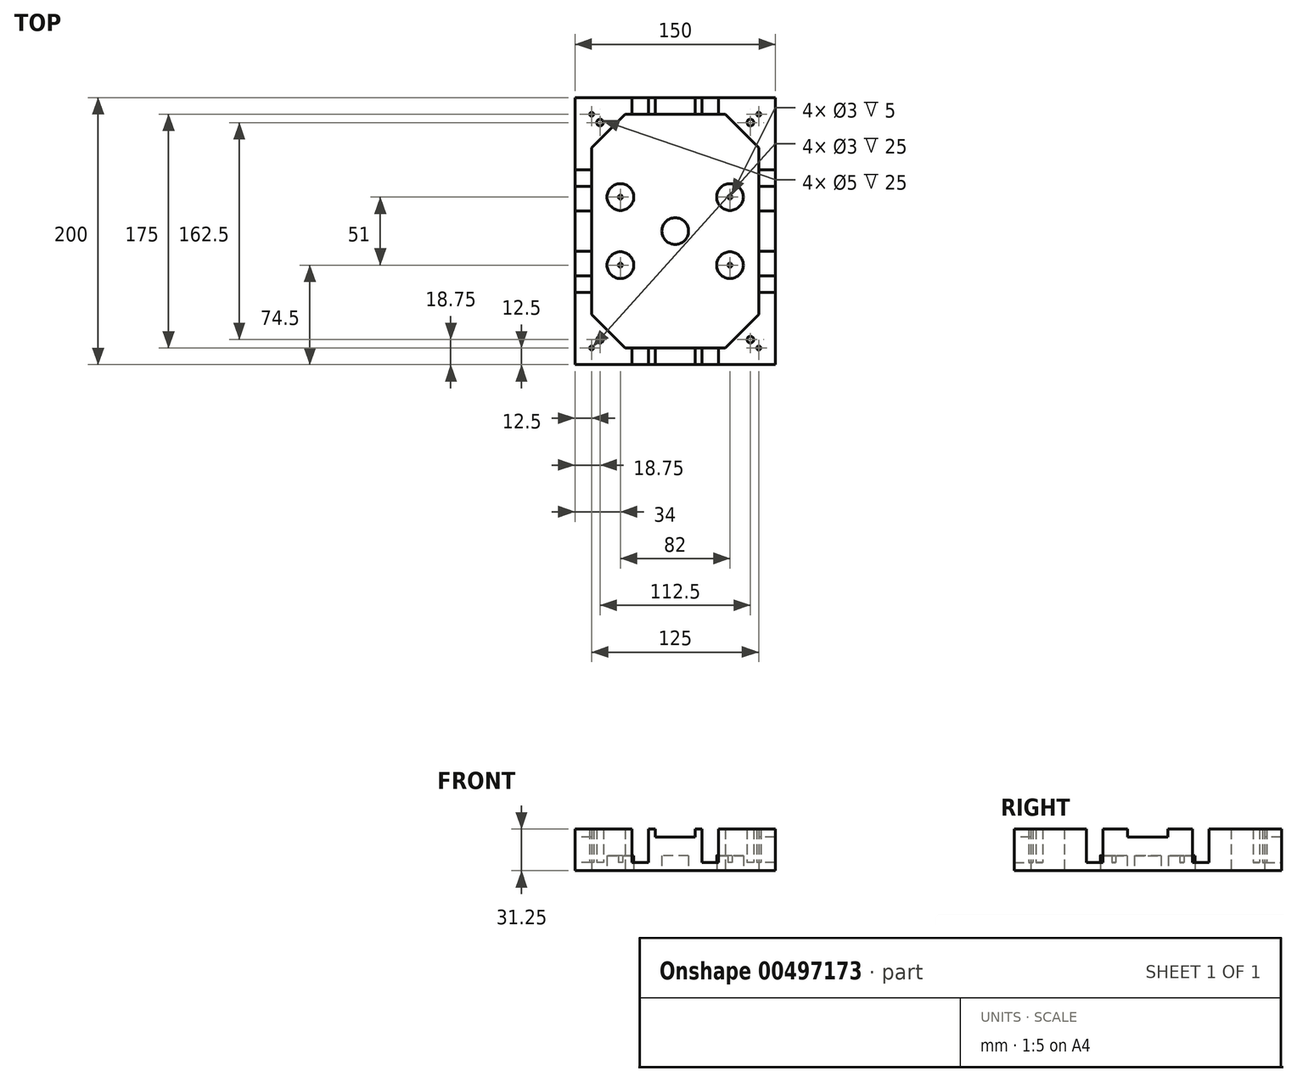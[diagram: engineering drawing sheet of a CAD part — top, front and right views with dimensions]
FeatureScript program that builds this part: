
annotation { "Feature Type Name" : "Feature", "Feature Type Description" : "" }
export const myFeature = defineFeature(function(context is Context, id is Id, definition is map)
    precondition{}
    {
        {
            var Q0;
            Q0=qCreatedBy(makeId("Top.planeOp"),FACE);
            var sketch = newSketch(context, id + "F0", { "sketchPlane" : qUnion([Q0])});
            skLineSegment(sketch, "E0.bottom", {"start": v(-75, 100) * mm, "end": v(75, 100) * mm});
            skLineSegment(sketch, "E0.top", {"start": v(-75, -100) * mm, "end": v(75, -100) * mm});
            skLineSegment(sketch, "E0.left", {"start": v(-75, 100) * mm, "end": v(-75, -100) * mm});
            skLineSegment(sketch, "E0.right", {"start": v(75, 100) * mm, "end": v(75, -100) * mm});
            skPoint(sketch, "E0.middle", {"position": v(0, 0) * mm});
            skLineSegment(sketch, "E1.bottom", {"start": v(-68.75, 93.75) * mm, "end": v(68.75, 93.75) * mm});
            skLineSegment(sketch, "E1.top", {"start": v(-68.75, -93.75) * mm, "end": v(68.75, -93.75) * mm});
            skLineSegment(sketch, "E1.left", {"start": v(-68.75, 93.75) * mm, "end": v(-68.75, -93.75) * mm});
            skLineSegment(sketch, "E1.right", {"start": v(68.75, 93.75) * mm, "end": v(68.75, -93.75) * mm});
            skLineSegment(sketch, "E2.bottom", {"start": v(-62.5, 87.5) * mm, "end": v(62.5, 87.5) * mm});
            skLineSegment(sketch, "E2.top", {"start": v(-62.5, -87.5) * mm, "end": v(62.5, -87.5) * mm});
            skLineSegment(sketch, "E2.left", {"start": v(-62.5, 87.5) * mm, "end": v(-62.5, -87.5) * mm});
            skLineSegment(sketch, "E2.right", {"start": v(62.5, 87.5) * mm, "end": v(62.5, -87.5) * mm});
            skLineSegment(sketch, "E3.bottom", {"start": v(-51, 35.5) * mm, "end": v(51, 35.5) * mm, "construction": true});
            skLineSegment(sketch, "E3.top", {"start": v(-51, -35.5) * mm, "end": v(51, -35.5) * mm, "construction": true});
            skLineSegment(sketch, "E3.left", {"start": v(-51, 35.5) * mm, "end": v(-51, -35.5) * mm, "construction": true});
            skLineSegment(sketch, "E3.right", {"start": v(51, 35.5) * mm, "end": v(51, -35.5) * mm, "construction": true});
            skPoint(sketch, "E4", {"position": v(37.5, 87.5) * mm});
            skPoint(sketch, "E5", {"position": v(37.5, -87.5) * mm});
            skPoint(sketch, "E6", {"position": v(-37.5, 87.5) * mm});
            skPoint(sketch, "E7", {"position": v(-37.5, -87.5) * mm});
            skPoint(sketch, "E8", {"position": v(-62.5, 62.5) * mm});
            skPoint(sketch, "E9", {"position": v(62.5, 62.5) * mm});
            skPoint(sketch, "E10", {"position": v(62.5, -62.5) * mm});
            skPoint(sketch, "E11", {"position": v(-62.5, -62.5) * mm});
            skPoint(sketch, "E12", {"position": v(-62.5, 87.5) * mm});
            skPoint(sketch, "E13", {"position": v(62.5, 87.5) * mm});
            skPoint(sketch, "E14", {"position": v(62.5, -87.5) * mm});
            skPoint(sketch, "E15", {"position": v(-62.5, -87.5) * mm});
            skLineSegment(sketch, "E16", {"start": v(-62.5, -62.5) * mm, "end": v(-37.5, -87.5) * mm});
            skLineSegment(sketch, "E17", {"start": v(37.5, -87.5) * mm, "end": v(62.5, -62.5) * mm});
            skLineSegment(sketch, "E18", {"start": v(62.5, 62.5) * mm, "end": v(37.5, 87.5) * mm});
            skLineSegment(sketch, "E19", {"start": v(-37.5, 87.5) * mm, "end": v(-62.5, 62.5) * mm});
            skPoint(sketch, "E20", {"position": v(-50, 75) * mm});
            skPoint(sketch, "E21", {"position": v(50, 75) * mm});
            skPoint(sketch, "E22", {"position": v(50, -75) * mm});
            skPoint(sketch, "E23", {"position": v(-50, -75) * mm});
            skLineSegment(sketch, "E24", {"start": v(-62.5, 87.5) * mm, "end": v(-50, 75) * mm, "construction": true});
            skLineSegment(sketch, "E25", {"start": v(62.5, 87.5) * mm, "end": v(50, 75) * mm, "construction": true});
            skLineSegment(sketch, "E26", {"start": v(62.5, -87.5) * mm, "end": v(50, -75) * mm, "construction": true});
            skLineSegment(sketch, "E27", {"start": v(-62.5, -87.5) * mm, "end": v(-50, -75) * mm, "construction": true});
            skPoint(sketch, "E28", {"position": v(-56.25, 81.25) * mm});
            skPoint(sketch, "E29", {"position": v(56.25, 81.25) * mm});
            skPoint(sketch, "E30", {"position": v(56.25, -81.25) * mm});
            skPoint(sketch, "E31", {"position": v(-56.25, -81.25) * mm});
            skLineSegment(sketch, "E32.bottom", {"start": v(-51, 35.5) * mm, "end": v(-41, 35.5) * mm, "construction": true});
            skLineSegment(sketch, "E32.top", {"start": v(-51, 25.5) * mm, "end": v(-41, 25.5) * mm, "construction": true});
            skLineSegment(sketch, "E32.left", {"start": v(-51, 35.5) * mm, "end": v(-51, 25.5) * mm, "construction": true});
            skLineSegment(sketch, "E32.right", {"start": v(-41, 35.5) * mm, "end": v(-41, 25.5) * mm, "construction": true});
            skLineSegment(sketch, "E33.bottom", {"start": v(51, 35.5) * mm, "end": v(41, 35.5) * mm, "construction": true});
            skLineSegment(sketch, "E33.top", {"start": v(51, 25.5) * mm, "end": v(41, 25.5) * mm, "construction": true});
            skLineSegment(sketch, "E33.left", {"start": v(51, 35.5) * mm, "end": v(51, 25.5) * mm, "construction": true});
            skLineSegment(sketch, "E33.right", {"start": v(41, 35.5) * mm, "end": v(41, 25.5) * mm, "construction": true});
            skLineSegment(sketch, "E34.bottom", {"start": v(-51, -35.5) * mm, "end": v(-41, -35.5) * mm, "construction": true});
            skLineSegment(sketch, "E34.top", {"start": v(-51, -25.5) * mm, "end": v(-41, -25.5) * mm, "construction": true});
            skLineSegment(sketch, "E34.left", {"start": v(-51, -35.5) * mm, "end": v(-51, -25.5) * mm, "construction": true});
            skLineSegment(sketch, "E34.right", {"start": v(-41, -35.5) * mm, "end": v(-41, -25.5) * mm, "construction": true});
            skLineSegment(sketch, "E35.bottom", {"start": v(51, -35.5) * mm, "end": v(41, -35.5) * mm, "construction": true});
            skLineSegment(sketch, "E35.top", {"start": v(51, -25.5) * mm, "end": v(41, -25.5) * mm, "construction": true});
            skLineSegment(sketch, "E35.left", {"start": v(51, -35.5) * mm, "end": v(51, -25.5) * mm, "construction": true});
            skLineSegment(sketch, "E35.right", {"start": v(41, -35.5) * mm, "end": v(41, -25.5) * mm, "construction": true});
            skPoint(sketch, "E36", {"position": v(-41, 25.5) * mm});
            skPoint(sketch, "E37", {"position": v(41, 25.5) * mm});
            skPoint(sketch, "E38", {"position": v(41, -25.5) * mm});
            skPoint(sketch, "E39", {"position": v(-41, -25.5) * mm});
            skCircle(sketch, "E40", {"center": v(41, 25.5) * mm, "radius": 10 * mm});
            skCircle(sketch, "E41", {"center": v(-41, 25.5) * mm, "radius": 10 * mm});
            skCircle(sketch, "E42", {"center": v(-41, -25.5) * mm, "radius": 10 * mm});
            skCircle(sketch, "E43", {"center": v(41, -25.5) * mm, "radius": 10 * mm});
            skCircle(sketch, "E44", {"center": v(41, 25.5) * mm, "radius": 1.5 * mm});
            skCircle(sketch, "E45", {"center": v(-41, 25.5) * mm, "radius": 1.5 * mm});
            skCircle(sketch, "E46", {"center": v(-41, -25.5) * mm, "radius": 1.5 * mm});
            skCircle(sketch, "E47", {"center": v(41, -25.5) * mm, "radius": 1.5 * mm});
            skCircle(sketch, "E48", {"center": v(0, 0) * mm, "radius": 10 * mm});
            skCircle(sketch, "E49", {"center": v(-62.5, 87.5) * mm, "radius": 1.5 * mm});
            skCircle(sketch, "E50", {"center": v(62.5, 87.5) * mm, "radius": 1.5 * mm});
            skCircle(sketch, "E51", {"center": v(62.5, -87.5) * mm, "radius": 1.5 * mm});
            skCircle(sketch, "E52", {"center": v(-62.5, -87.5) * mm, "radius": 1.5 * mm});
            skCircle(sketch, "E53", {"center": v(-56.25, -81.25) * mm, "radius": 2.5 * mm});
            skCircle(sketch, "E54", {"center": v(56.25, -81.25) * mm, "radius": 2.5 * mm});
            skCircle(sketch, "E55", {"center": v(56.25, 81.25) * mm, "radius": 2.5 * mm});
            skCircle(sketch, "E56", {"center": v(-56.25, 81.25) * mm, "radius": 2.5 * mm});
            skPoint(sketch, "E57", {"position": v(0, 74.98) * mm});
            skPoint(sketch, "E58", {"position": v(15, -87.5) * mm});
            skPoint(sketch, "E59", {"position": v(15, -100) * mm});
            skPoint(sketch, "E60", {"position": v(-15, -100) * mm});
            skPoint(sketch, "E61", {"position": v(-15, -87.5) * mm});
            skLineSegment(sketch, "E62", {"start": v(-15, -87.5) * mm, "end": v(-15, -100) * mm});
            skLineSegment(sketch, "E63", {"start": v(15, -87.5) * mm, "end": v(15, -100) * mm});
            skPoint(sketch, "E64", {"position": v(32.5, -87.5) * mm});
            skPoint(sketch, "E65", {"position": v(32.5, -100) * mm});
            skPoint(sketch, "E66", {"position": v(20, -100) * mm});
            skPoint(sketch, "E67", {"position": v(20, -87.5) * mm});
            skPoint(sketch, "E68", {"position": v(-20, -87.5) * mm});
            skPoint(sketch, "E69", {"position": v(-32.5, -87.5) * mm});
            skPoint(sketch, "E70", {"position": v(-32.5, -100) * mm});
            skPoint(sketch, "E71", {"position": v(-20, -100) * mm});
            skPoint(sketch, "E72", {"position": v(-15, 87.5) * mm});
            skPoint(sketch, "E73", {"position": v(-20, 87.5) * mm});
            skPoint(sketch, "E74", {"position": v(-32.5, 87.5) * mm});
            skPoint(sketch, "E75", {"position": v(32.5, 87.5) * mm});
            skPoint(sketch, "E76", {"position": v(20, 87.5) * mm});
            skPoint(sketch, "E77", {"position": v(15, 87.5) * mm});
            skPoint(sketch, "E78", {"position": v(-32.5, 100) * mm});
            skPoint(sketch, "E79", {"position": v(-20, 100) * mm});
            skPoint(sketch, "E80", {"position": v(-15, 100) * mm});
            skPoint(sketch, "E81", {"position": v(15, 100) * mm});
            skPoint(sketch, "E82", {"position": v(20, 100) * mm});
            skPoint(sketch, "E83", {"position": v(32.5, 100) * mm});
            skPoint(sketch, "E84", {"position": v(75, 15) * mm});
            skPoint(sketch, "E85", {"position": v(75, -15) * mm});
            skPoint(sketch, "E86", {"position": v(-75, -15) * mm});
            skPoint(sketch, "E87", {"position": v(-75, 15) * mm});
            skPoint(sketch, "E88", {"position": v(62.5, 15) * mm});
            skPoint(sketch, "E89", {"position": v(62.5, -15) * mm});
            skPoint(sketch, "E90", {"position": v(-62.5, 15) * mm});
            skPoint(sketch, "E91", {"position": v(-62.5, -15) * mm});
            skLineSegment(sketch, "E92", {"start": v(-32.5, 100) * mm, "end": v(-32.5, 87.5) * mm});
            skLineSegment(sketch, "E93", {"start": v(-20, 100) * mm, "end": v(-20, 87.5) * mm});
            skLineSegment(sketch, "E94", {"start": v(-15, 100) * mm, "end": v(-15, 87.5) * mm});
            skLineSegment(sketch, "E95", {"start": v(15, 100) * mm, "end": v(15, 87.5) * mm});
            skLineSegment(sketch, "E96", {"start": v(20, 100) * mm, "end": v(20, 87.5) * mm});
            skLineSegment(sketch, "E97", {"start": v(32.5, 100) * mm, "end": v(32.5, 87.5) * mm});
            skLineSegment(sketch, "E98", {"start": v(75, 15) * mm, "end": v(62.5, 15) * mm});
            skLineSegment(sketch, "E99", {"start": v(75, -15) * mm, "end": v(62.5, -15) * mm});
            skLineSegment(sketch, "E100", {"start": v(-62.5, 15) * mm, "end": v(-75, 15) * mm});
            skLineSegment(sketch, "E101", {"start": v(-62.5, -15) * mm, "end": v(-75, -15) * mm});
            skLineSegment(sketch, "E102", {"start": v(-32.5, -87.5) * mm, "end": v(-32.5, -100) * mm});
            skLineSegment(sketch, "E103", {"start": v(-20, -87.5) * mm, "end": v(-20, -100) * mm});
            skLineSegment(sketch, "E104", {"start": v(20, -87.5) * mm, "end": v(20, -100) * mm});
            skLineSegment(sketch, "E105", {"start": v(32.5, -87.5) * mm, "end": v(32.5, -100) * mm});
            skPoint(sketch, "E106", {"position": v(62.5, 46) * mm});
            skPoint(sketch, "E107", {"position": v(62.5, 33.5) * mm});
            skPoint(sketch, "E108", {"position": v(62.5, -46) * mm});
            skPoint(sketch, "E109", {"position": v(62.5, -33.5) * mm});
            skPoint(sketch, "E110", {"position": v(-62.5, 46) * mm});
            skPoint(sketch, "E111", {"position": v(-62.5, 33.5) * mm});
            skPoint(sketch, "E112", {"position": v(-62.5, -33.5) * mm});
            skPoint(sketch, "E113", {"position": v(-62.5, -46) * mm});
            skPoint(sketch, "E114", {"position": v(-75, 46) * mm});
            skPoint(sketch, "E115", {"position": v(-75, 33.5) * mm});
            skPoint(sketch, "E116", {"position": v(-75, -33.5) * mm});
            skPoint(sketch, "E117", {"position": v(-75, -46) * mm});
            skPoint(sketch, "E118", {"position": v(75, -46) * mm});
            skPoint(sketch, "E119", {"position": v(75, -33.5) * mm});
            skPoint(sketch, "E120", {"position": v(75, 46) * mm});
            skPoint(sketch, "E121", {"position": v(75, 33.5) * mm});
            skLineSegment(sketch, "E122", {"start": v(-75, 46) * mm, "end": v(-62.5, 46) * mm});
            skLineSegment(sketch, "E123", {"start": v(-75, 33.5) * mm, "end": v(-62.5, 33.5) * mm});
            skLineSegment(sketch, "E124", {"start": v(-75, -33.5) * mm, "end": v(-62.5, -33.5) * mm});
            skLineSegment(sketch, "E125", {"start": v(-75, -46) * mm, "end": v(-62.5, -46) * mm});
            skLineSegment(sketch, "E126", {"start": v(62.5, -33.5) * mm, "end": v(75, -33.5) * mm});
            skLineSegment(sketch, "E127", {"start": v(62.5, -46) * mm, "end": v(75, -46) * mm});
            skLineSegment(sketch, "E128", {"start": v(62.5, 46) * mm, "end": v(75, 46) * mm});
            skPoint(sketch, "E129", {"position": v(-32.5, 93.75) * mm});
            skPoint(sketch, "E130", {"position": v(-20, 93.75) * mm});
            skPoint(sketch, "E131", {"position": v(-15, 93.75) * mm});
            skPoint(sketch, "E132", {"position": v(15, 93.75) * mm});
            skPoint(sketch, "E133", {"position": v(20, 93.75) * mm});
            skPoint(sketch, "E134", {"position": v(32.5, 93.75) * mm});
            skPoint(sketch, "E135", {"position": v(68.75, 46) * mm});
            skPoint(sketch, "E136", {"position": v(68.75, 33.5) * mm});
            skPoint(sketch, "E137", {"position": v(68.75, 15) * mm});
            skPoint(sketch, "E138", {"position": v(68.75, -15) * mm});
            skPoint(sketch, "E139", {"position": v(68.75, -33.5) * mm});
            skPoint(sketch, "E140", {"position": v(68.75, -46) * mm});
            skPoint(sketch, "E141", {"position": v(32.5, -93.75) * mm});
            skPoint(sketch, "E142", {"position": v(20, -93.75) * mm});
            skPoint(sketch, "E143", {"position": v(15, -93.75) * mm});
            skPoint(sketch, "E144", {"position": v(-15, -93.75) * mm});
            skPoint(sketch, "E145", {"position": v(-20, -93.75) * mm});
            skPoint(sketch, "E146", {"position": v(-32.5, -93.75) * mm});
            skPoint(sketch, "E147", {"position": v(-68.75, -46) * mm});
            skPoint(sketch, "E148", {"position": v(-68.75, -33.5) * mm});
            skPoint(sketch, "E149", {"position": v(-68.75, -15) * mm});
            skPoint(sketch, "E150", {"position": v(-68.75, 15) * mm});
            skPoint(sketch, "E151", {"position": v(-68.75, 33.5) * mm});
            skPoint(sketch, "E152", {"position": v(-68.75, 46) * mm});
            skLineSegment(sketch, "E153", {"start": v(75, 33.5) * mm, "end": v(62.5, 33.5) * mm});
            skSolve(sketch);
        }
        {
            var Q0;
            Q0=makeQuery(id+"F0.imprint","IMPRINT",FACE,{"disambiguationData":[TD([[makeQuery(id+"F0.imprint","IMPRINT",EDGE,{"derivedFrom":sQuery(id+"F0.wireOp",EDGE,"E43")}),1.0]])]});
            var Q1;
            Q1=makeQuery(id+"F0.imprint","IMPRINT",FACE,{"disambiguationData":[TD([[makeQuery(id+"F0.imprint","IMPRINT",EDGE,{"derivedFrom":sQuery(id+"F0.wireOp",EDGE,"E42")}),1.0]])]});
            var Q2;
            {var subQ5=sQuery(id+"F0.wireOp",EDGE,"E17");Q2=makeQuery(id+"F0.imprint","IMPRINT",FACE,{"disambiguationData":[TD([[makeQuery(id+"F0.imprint","IMPRINT",EDGE,{"derivedFrom":subQ5}),-1.0]])]});}
            var Q3;
            {var subQ0=sQuery(id+"F0.wireOp",EDGE,"E122");var subQ1=sQuery(id+"F0.wireOp",EDGE,"E0.left");var subQ2=makeQuery(id+"F0.imprint","INTERSECT",VERTEX,{"derivedFrom":[subQ1,subQ0]});Q3=makeQuery(id+"F0.imprint","IMPRINT",FACE,{"disambiguationData":[TD([[makeQuery(id+"F0.imprint","IMPRINT",EDGE,{"disambiguationData":[TD([[subQ2,-1.0]])],"derivedFrom":subQ1}),1.0]])]});}
            var Q4;
            {var subQ0=sQuery(id+"F0.wireOp",EDGE,"E124");var subQ1=sQuery(id+"F0.wireOp",EDGE,"E0.left");var subQ2=makeQuery(id+"F0.imprint","INTERSECT",VERTEX,{"derivedFrom":[subQ1,subQ0]});Q4=makeQuery(id+"F0.imprint","IMPRINT",FACE,{"disambiguationData":[TD([[makeQuery(id+"F0.imprint","IMPRINT",EDGE,{"disambiguationData":[TD([[subQ2,-1.0]])],"derivedFrom":subQ1}),1.0]])]});}
            var Q5;
            {var subQ0=sQuery(id+"F0.wireOp",EDGE,"E62");var subQ1=sQuery(id+"F0.wireOp",EDGE,"E1.top");var subQ2=makeQuery(id+"F0.imprint","INTERSECT",VERTEX,{"derivedFrom":[subQ1,subQ0]});Q5=makeQuery(id+"F0.imprint","IMPRINT",FACE,{"disambiguationData":[TD([[makeQuery(id+"F0.imprint","IMPRINT",EDGE,{"disambiguationData":[TD([[subQ2,-1.0]])],"derivedFrom":subQ1}),1.0]])]});}
            var Q6;
            {var subQ0=sQuery(id+"F0.wireOp",EDGE,"E100");var subQ1=sQuery(id+"F0.wireOp",EDGE,"E0.left");var subQ2=makeQuery(id+"F0.imprint","INTERSECT",VERTEX,{"derivedFrom":[subQ1,subQ0]});Q6=makeQuery(id+"F0.imprint","IMPRINT",FACE,{"disambiguationData":[TD([[makeQuery(id+"F0.imprint","IMPRINT",EDGE,{"disambiguationData":[TD([[subQ2,-1.0]])],"derivedFrom":subQ1}),1.0]])]});}
            var Q7;
            {var subQ0=sQuery(id+"F0.wireOp",EDGE,"E62");var subQ1=sQuery(id+"F0.wireOp",EDGE,"E0.top");var subQ2=makeQuery(id+"F0.imprint","INTERSECT",VERTEX,{"derivedFrom":[subQ1,subQ0]});Q7=makeQuery(id+"F0.imprint","IMPRINT",FACE,{"disambiguationData":[TD([[makeQuery(id+"F0.imprint","IMPRINT",EDGE,{"disambiguationData":[TD([[subQ2,1.0]])],"derivedFrom":subQ1}),1.0]])]});}
            var Q8;
            {var subQ0=sQuery(id+"F0.wireOp",EDGE,"E99");var subQ1=sQuery(id+"F0.wireOp",EDGE,"E0.right");var subQ2=makeQuery(id+"F0.imprint","INTERSECT",VERTEX,{"derivedFrom":[subQ1,subQ0]});Q8=makeQuery(id+"F0.imprint","IMPRINT",FACE,{"disambiguationData":[TD([[makeQuery(id+"F0.imprint","IMPRINT",EDGE,{"disambiguationData":[TD([[subQ2,-1.0]])],"derivedFrom":subQ1}),-1.0]])]});}
            var Q9;
            {var subQ0=sQuery(id+"F0.wireOp",EDGE,"E98");var subQ1=sQuery(id+"F0.wireOp",EDGE,"E0.right");var subQ2=makeQuery(id+"F0.imprint","INTERSECT",VERTEX,{"derivedFrom":[subQ1,subQ0]});Q9=makeQuery(id+"F0.imprint","IMPRINT",FACE,{"disambiguationData":[TD([[makeQuery(id+"F0.imprint","IMPRINT",EDGE,{"disambiguationData":[TD([[subQ2,-1.0]])],"derivedFrom":subQ1}),-1.0]])]});}
            var Q10;
            {var subQ0=sQuery(id+"F0.wireOp",EDGE,"E94");var subQ1=sQuery(id+"F0.wireOp",EDGE,"E1.bottom");var subQ2=makeQuery(id+"F0.imprint","INTERSECT",VERTEX,{"derivedFrom":[subQ1,subQ0]});Q10=makeQuery(id+"F0.imprint","IMPRINT",FACE,{"disambiguationData":[TD([[makeQuery(id+"F0.imprint","IMPRINT",EDGE,{"disambiguationData":[TD([[subQ2,-1.0]])],"derivedFrom":subQ1}),-1.0]])]});}
            var Q11;
            {var subQ23=sQuery(id+"F0.wireOp",EDGE,"E16");Q11=makeQuery(id+"F0.imprint","IMPRINT",FACE,{"disambiguationData":[TD([[makeQuery(id+"F0.imprint","IMPRINT",EDGE,{"derivedFrom":subQ23}),1.0]])]});}
            var Q12;
            {var subQ0=sQuery(id+"F0.wireOp",EDGE,"E100");var subQ1=sQuery(id+"F0.wireOp",EDGE,"E0.left");var subQ2=makeQuery(id+"F0.imprint","INTERSECT",VERTEX,{"derivedFrom":[subQ1,subQ0]});Q12=makeQuery(id+"F0.imprint","IMPRINT",FACE,{"disambiguationData":[TD([[makeQuery(id+"F0.imprint","IMPRINT",EDGE,{"disambiguationData":[TD([[subQ2,1.0]])],"derivedFrom":subQ1}),1.0]])]});}
            var Q13;
            {var subQ0=sQuery(id+"F0.wireOp",EDGE,"E96");var subQ1=sQuery(id+"F0.wireOp",EDGE,"E0.bottom");var subQ2=makeQuery(id+"F0.imprint","INTERSECT",VERTEX,{"derivedFrom":[subQ1,subQ0]});Q13=makeQuery(id+"F0.imprint","IMPRINT",FACE,{"disambiguationData":[TD([[makeQuery(id+"F0.imprint","IMPRINT",EDGE,{"disambiguationData":[TD([[subQ2,-1.0]])],"derivedFrom":subQ1}),-1.0]])]});}
            var Q14;
            Q14=makeQuery(id+"F0.imprint","IMPRINT",FACE,{"disambiguationData":[TD([[makeQuery(id+"F0.imprint","IMPRINT",EDGE,{"derivedFrom":sQuery(id+"F0.wireOp",EDGE,"E41")}),1.0]])]});
            var Q15;
            {var subQ5=sQuery(id+"F0.wireOp",EDGE,"E16");Q15=makeQuery(id+"F0.imprint","IMPRINT",FACE,{"disambiguationData":[TD([[makeQuery(id+"F0.imprint","IMPRINT",EDGE,{"derivedFrom":subQ5}),-1.0]])]});}
            var Q16;
            {var subQ0=sQuery(id+"F0.wireOp",EDGE,"E95");var subQ1=sQuery(id+"F0.wireOp",EDGE,"E0.bottom");var subQ2=makeQuery(id+"F0.imprint","INTERSECT",VERTEX,{"derivedFrom":[subQ1,subQ0]});Q16=makeQuery(id+"F0.imprint","IMPRINT",FACE,{"disambiguationData":[TD([[makeQuery(id+"F0.imprint","IMPRINT",EDGE,{"disambiguationData":[TD([[subQ2,-1.0]])],"derivedFrom":subQ1}),-1.0]])]});}
            var Q17;
            {var subQ0=sQuery(id+"F0.wireOp",EDGE,"E102");var subQ1=sQuery(id+"F0.wireOp",EDGE,"E0.top");var subQ2=makeQuery(id+"F0.imprint","INTERSECT",VERTEX,{"derivedFrom":[subQ1,subQ0]});Q17=makeQuery(id+"F0.imprint","IMPRINT",FACE,{"disambiguationData":[TD([[makeQuery(id+"F0.imprint","IMPRINT",EDGE,{"disambiguationData":[TD([[subQ2,-1.0]])],"derivedFrom":subQ1}),1.0]])]});}
            var Q18;
            {var subQ0=sQuery(id+"F0.wireOp",EDGE,"E101");var subQ1=sQuery(id+"F0.wireOp",EDGE,"E1.left");var subQ2=makeQuery(id+"F0.imprint","INTERSECT",VERTEX,{"derivedFrom":[subQ1,subQ0]});Q18=makeQuery(id+"F0.imprint","IMPRINT",FACE,{"disambiguationData":[TD([[makeQuery(id+"F0.imprint","IMPRINT",EDGE,{"disambiguationData":[TD([[subQ2,-1.0]])],"derivedFrom":subQ1}),1.0]])]});}
            var Q19;
            {var subQ0=sQuery(id+"F0.wireOp",EDGE,"E99");var subQ1=sQuery(id+"F0.wireOp",EDGE,"E1.right");var subQ2=makeQuery(id+"F0.imprint","INTERSECT",VERTEX,{"derivedFrom":[subQ1,subQ0]});Q19=makeQuery(id+"F0.imprint","IMPRINT",FACE,{"disambiguationData":[TD([[makeQuery(id+"F0.imprint","IMPRINT",EDGE,{"disambiguationData":[TD([[subQ2,-1.0]])],"derivedFrom":subQ1}),-1.0]])]});}
            var Q20;
            {var subQ0=sQuery(id+"F0.wireOp",EDGE,"E103");var subQ1=sQuery(id+"F0.wireOp",EDGE,"E1.top");var subQ2=makeQuery(id+"F0.imprint","INTERSECT",VERTEX,{"derivedFrom":[subQ1,subQ0]});Q20=makeQuery(id+"F0.imprint","IMPRINT",FACE,{"disambiguationData":[TD([[makeQuery(id+"F0.imprint","IMPRINT",EDGE,{"disambiguationData":[TD([[subQ2,-1.0]])],"derivedFrom":subQ1}),1.0]])]});}
            var Q21;
            {var subQ0=sQuery(id+"F0.wireOp",EDGE,"E153");var subQ1=sQuery(id+"F0.wireOp",EDGE,"E1.right");var subQ2=makeQuery(id+"F0.imprint","INTERSECT",VERTEX,{"derivedFrom":[subQ1,subQ0]});Q21=makeQuery(id+"F0.imprint","IMPRINT",FACE,{"disambiguationData":[TD([[makeQuery(id+"F0.imprint","IMPRINT",EDGE,{"disambiguationData":[TD([[subQ2,-1.0]])],"derivedFrom":subQ1}),-1.0]])]});}
            var Q22;
            {var subQ7=sQuery(id+"F0.wireOp",EDGE,"E0.right");var subQ8=sQuery(id+"F0.wireOp",EDGE,"E0.top");var subQ9=makeQuery(id+"F0.imprint","INTERSECT",VERTEX,{"derivedFrom":[subQ8,subQ7]});Q22=makeQuery(id+"F0.imprint","IMPRINT",FACE,{"disambiguationData":[TD([[makeQuery(id+"F0.imprint","IMPRINT",EDGE,{"disambiguationData":[TD([[subQ9,1.0]])],"derivedFrom":subQ8}),1.0]])]});}
            var Q23;
            {var subQ0=sQuery(id+"F0.wireOp",EDGE,"E92");var subQ1=sQuery(id+"F0.wireOp",EDGE,"E1.bottom");var subQ2=makeQuery(id+"F0.imprint","INTERSECT",VERTEX,{"derivedFrom":[subQ1,subQ0]});Q23=makeQuery(id+"F0.imprint","IMPRINT",FACE,{"disambiguationData":[TD([[makeQuery(id+"F0.imprint","IMPRINT",EDGE,{"disambiguationData":[TD([[subQ2,-1.0]])],"derivedFrom":subQ1}),-1.0]])]});}
            var Q24;
            {var subQ0=sQuery(id+"F0.wireOp",EDGE,"E124");var subQ1=sQuery(id+"F0.wireOp",EDGE,"E1.left");var subQ2=makeQuery(id+"F0.imprint","INTERSECT",VERTEX,{"derivedFrom":[subQ1,subQ0]});Q24=makeQuery(id+"F0.imprint","IMPRINT",FACE,{"disambiguationData":[TD([[makeQuery(id+"F0.imprint","IMPRINT",EDGE,{"disambiguationData":[TD([[subQ2,-1.0]])],"derivedFrom":subQ1}),1.0]])]});}
            var Q25;
            {var subQ5=sQuery(id+"F0.wireOp",EDGE,"E0.right");var subQ9=sQuery(id+"F0.wireOp",EDGE,"E0.bottom");var subQ10=makeQuery(id+"F0.imprint","INTERSECT",VERTEX,{"derivedFrom":[subQ9,subQ5]});Q25=makeQuery(id+"F0.imprint","IMPRINT",FACE,{"disambiguationData":[TD([[makeQuery(id+"F0.imprint","IMPRINT",EDGE,{"disambiguationData":[TD([[subQ10,1.0]])],"derivedFrom":subQ9}),-1.0]])]});}
            var Q26;
            {var subQ0=sQuery(id+"F0.wireOp",EDGE,"E18");Q26=makeQuery(id+"F0.imprint","IMPRINT",FACE,{"disambiguationData":[TD([[makeQuery(id+"F0.imprint","IMPRINT",EDGE,{"derivedFrom":subQ0}),-1.0]])]});}
            var Q27;
            {var subQ7=sQuery(id+"F0.wireOp",EDGE,"E0.left");var subQ8=sQuery(id+"F0.wireOp",EDGE,"E0.bottom");var subQ9=makeQuery(id+"F0.imprint","INTERSECT",VERTEX,{"derivedFrom":[subQ8,subQ7]});Q27=makeQuery(id+"F0.imprint","IMPRINT",FACE,{"disambiguationData":[TD([[makeQuery(id+"F0.imprint","IMPRINT",EDGE,{"disambiguationData":[TD([[subQ9,-1.0]])],"derivedFrom":subQ8}),-1.0]])]});}
            var Q28;
            {var subQ8=sQuery(id+"F0.wireOp",EDGE,"E1.left");var subQ9=sQuery(id+"F0.wireOp",EDGE,"E1.bottom");var subQ10=makeQuery(id+"F0.imprint","INTERSECT",VERTEX,{"derivedFrom":[subQ9,subQ8]});Q28=makeQuery(id+"F0.imprint","IMPRINT",FACE,{"disambiguationData":[TD([[makeQuery(id+"F0.imprint","IMPRINT",EDGE,{"disambiguationData":[TD([[subQ10,-1.0]])],"derivedFrom":subQ9}),-1.0]])]});}
            var Q29;
            {var subQ0=sQuery(id+"F0.wireOp",EDGE,"E102");var subQ1=sQuery(id+"F0.wireOp",EDGE,"E1.top");var subQ2=makeQuery(id+"F0.imprint","INTERSECT",VERTEX,{"derivedFrom":[subQ1,subQ0]});Q29=makeQuery(id+"F0.imprint","IMPRINT",FACE,{"disambiguationData":[TD([[makeQuery(id+"F0.imprint","IMPRINT",EDGE,{"disambiguationData":[TD([[subQ2,-1.0]])],"derivedFrom":subQ1}),1.0]])]});}
            var Q30;
            {var subQ0=sQuery(id+"F0.wireOp",EDGE,"E93");var subQ1=sQuery(id+"F0.wireOp",EDGE,"E1.bottom");var subQ2=makeQuery(id+"F0.imprint","INTERSECT",VERTEX,{"derivedFrom":[subQ1,subQ0]});Q30=makeQuery(id+"F0.imprint","IMPRINT",FACE,{"disambiguationData":[TD([[makeQuery(id+"F0.imprint","IMPRINT",EDGE,{"disambiguationData":[TD([[subQ2,-1.0]])],"derivedFrom":subQ1}),-1.0]])]});}
            var Q31;
            {var subQ0=sQuery(id+"F0.wireOp",EDGE,"E63");var subQ1=sQuery(id+"F0.wireOp",EDGE,"E1.top");var subQ2=makeQuery(id+"F0.imprint","INTERSECT",VERTEX,{"derivedFrom":[subQ1,subQ0]});Q31=makeQuery(id+"F0.imprint","IMPRINT",FACE,{"disambiguationData":[TD([[makeQuery(id+"F0.imprint","IMPRINT",EDGE,{"disambiguationData":[TD([[subQ2,-1.0]])],"derivedFrom":subQ1}),1.0]])]});}
            var Q32;
            {var subQ0=sQuery(id+"F0.wireOp",EDGE,"E100");var subQ1=sQuery(id+"F0.wireOp",EDGE,"E1.left");var subQ2=makeQuery(id+"F0.imprint","INTERSECT",VERTEX,{"derivedFrom":[subQ1,subQ0]});Q32=makeQuery(id+"F0.imprint","IMPRINT",FACE,{"disambiguationData":[TD([[makeQuery(id+"F0.imprint","IMPRINT",EDGE,{"disambiguationData":[TD([[subQ2,-1.0]])],"derivedFrom":subQ1}),1.0]])]});}
            var Q33;
            {var subQ0=sQuery(id+"F0.wireOp",EDGE,"E62");var subQ1=sQuery(id+"F0.wireOp",EDGE,"E0.top");var subQ2=makeQuery(id+"F0.imprint","INTERSECT",VERTEX,{"derivedFrom":[subQ1,subQ0]});Q33=makeQuery(id+"F0.imprint","IMPRINT",FACE,{"disambiguationData":[TD([[makeQuery(id+"F0.imprint","IMPRINT",EDGE,{"disambiguationData":[TD([[subQ2,-1.0]])],"derivedFrom":subQ1}),1.0]])]});}
            var Q34;
            {var subQ0=sQuery(id+"F0.wireOp",EDGE,"E98");var subQ1=sQuery(id+"F0.wireOp",EDGE,"E0.right");var subQ2=makeQuery(id+"F0.imprint","INTERSECT",VERTEX,{"derivedFrom":[subQ1,subQ0]});Q34=makeQuery(id+"F0.imprint","IMPRINT",FACE,{"disambiguationData":[TD([[makeQuery(id+"F0.imprint","IMPRINT",EDGE,{"disambiguationData":[TD([[subQ2,1.0]])],"derivedFrom":subQ1}),-1.0]])]});}
            var Q35;
            {var subQ0=sQuery(id+"F0.wireOp",EDGE,"E98");var subQ1=sQuery(id+"F0.wireOp",EDGE,"E1.right");var subQ2=makeQuery(id+"F0.imprint","INTERSECT",VERTEX,{"derivedFrom":[subQ1,subQ0]});Q35=makeQuery(id+"F0.imprint","IMPRINT",FACE,{"disambiguationData":[TD([[makeQuery(id+"F0.imprint","IMPRINT",EDGE,{"disambiguationData":[TD([[subQ2,-1.0]])],"derivedFrom":subQ1}),-1.0]])]});}
            var Q36;
            {var subQ0=sQuery(id+"F0.wireOp",EDGE,"E19");Q36=makeQuery(id+"F0.imprint","IMPRINT",FACE,{"disambiguationData":[TD([[makeQuery(id+"F0.imprint","IMPRINT",EDGE,{"derivedFrom":subQ0}),-1.0]])]});}
            var Q37;
            {var subQ0=sQuery(id+"F0.wireOp",EDGE,"E94");var subQ1=sQuery(id+"F0.wireOp",EDGE,"E0.bottom");var subQ2=makeQuery(id+"F0.imprint","INTERSECT",VERTEX,{"derivedFrom":[subQ1,subQ0]});Q37=makeQuery(id+"F0.imprint","IMPRINT",FACE,{"disambiguationData":[TD([[makeQuery(id+"F0.imprint","IMPRINT",EDGE,{"disambiguationData":[TD([[subQ2,-1.0]])],"derivedFrom":subQ1}),-1.0]])]});}
            var Q38;
            {var subQ7=sQuery(id+"F0.wireOp",EDGE,"E1.left");var subQ8=sQuery(id+"F0.wireOp",EDGE,"E1.top");var subQ9=makeQuery(id+"F0.imprint","INTERSECT",VERTEX,{"derivedFrom":[subQ8,subQ7]});Q38=makeQuery(id+"F0.imprint","IMPRINT",FACE,{"disambiguationData":[TD([[makeQuery(id+"F0.imprint","IMPRINT",EDGE,{"disambiguationData":[TD([[subQ9,-1.0]])],"derivedFrom":subQ8}),1.0]])]});}
            var Q39;
            {var subQ7=sQuery(id+"F0.wireOp",EDGE,"E0.left");var subQ8=sQuery(id+"F0.wireOp",EDGE,"E0.top");var subQ9=makeQuery(id+"F0.imprint","INTERSECT",VERTEX,{"derivedFrom":[subQ8,subQ7]});Q39=makeQuery(id+"F0.imprint","IMPRINT",FACE,{"disambiguationData":[TD([[makeQuery(id+"F0.imprint","IMPRINT",EDGE,{"disambiguationData":[TD([[subQ9,-1.0]])],"derivedFrom":subQ8}),1.0]])]});}
            var Q40;
            Q40=makeQuery(id+"F0.imprint","IMPRINT",FACE,{"disambiguationData":[TD([[makeQuery(id+"F0.imprint","IMPRINT",EDGE,{"derivedFrom":sQuery(id+"F0.wireOp",EDGE,"E40")}),1.0]])]});
            var Q41;
            {var subQ0=sQuery(id+"F0.wireOp",EDGE,"E122");var subQ1=sQuery(id+"F0.wireOp",EDGE,"E1.left");var subQ2=makeQuery(id+"F0.imprint","INTERSECT",VERTEX,{"derivedFrom":[subQ1,subQ0]});Q41=makeQuery(id+"F0.imprint","IMPRINT",FACE,{"disambiguationData":[TD([[makeQuery(id+"F0.imprint","IMPRINT",EDGE,{"disambiguationData":[TD([[subQ2,-1.0]])],"derivedFrom":subQ1}),1.0]])]});}
            var Q42;
            {var subQ0=sQuery(id+"F0.wireOp",EDGE,"E93");var subQ1=sQuery(id+"F0.wireOp",EDGE,"E0.bottom");var subQ2=makeQuery(id+"F0.imprint","INTERSECT",VERTEX,{"derivedFrom":[subQ1,subQ0]});Q42=makeQuery(id+"F0.imprint","IMPRINT",FACE,{"disambiguationData":[TD([[makeQuery(id+"F0.imprint","IMPRINT",EDGE,{"disambiguationData":[TD([[subQ2,-1.0]])],"derivedFrom":subQ1}),-1.0]])]});}
            var Q43;
            {var subQ0=sQuery(id+"F0.wireOp",EDGE,"E128");var subQ1=sQuery(id+"F0.wireOp",EDGE,"E1.right");var subQ2=makeQuery(id+"F0.imprint","INTERSECT",VERTEX,{"derivedFrom":[subQ1,subQ0]});Q43=makeQuery(id+"F0.imprint","IMPRINT",FACE,{"disambiguationData":[TD([[makeQuery(id+"F0.imprint","IMPRINT",EDGE,{"disambiguationData":[TD([[subQ2,-1.0]])],"derivedFrom":subQ1}),-1.0]])]});}
            var Q44;
            {var subQ0=sQuery(id+"F0.wireOp",EDGE,"E104");var subQ1=sQuery(id+"F0.wireOp",EDGE,"E0.top");var subQ2=makeQuery(id+"F0.imprint","INTERSECT",VERTEX,{"derivedFrom":[subQ1,subQ0]});Q44=makeQuery(id+"F0.imprint","IMPRINT",FACE,{"disambiguationData":[TD([[makeQuery(id+"F0.imprint","IMPRINT",EDGE,{"disambiguationData":[TD([[subQ2,-1.0]])],"derivedFrom":subQ1}),1.0]])]});}
            var Q45;
            {var subQ0=sQuery(id+"F0.wireOp",EDGE,"E96");var subQ1=sQuery(id+"F0.wireOp",EDGE,"E1.bottom");var subQ2=makeQuery(id+"F0.imprint","INTERSECT",VERTEX,{"derivedFrom":[subQ1,subQ0]});Q45=makeQuery(id+"F0.imprint","IMPRINT",FACE,{"disambiguationData":[TD([[makeQuery(id+"F0.imprint","IMPRINT",EDGE,{"disambiguationData":[TD([[subQ2,-1.0]])],"derivedFrom":subQ1}),-1.0]])]});}
            var Q46;
            {var subQ0=sQuery(id+"F0.wireOp",EDGE,"E126");var subQ1=sQuery(id+"F0.wireOp",EDGE,"E0.right");var subQ2=makeQuery(id+"F0.imprint","INTERSECT",VERTEX,{"derivedFrom":[subQ1,subQ0]});Q46=makeQuery(id+"F0.imprint","IMPRINT",FACE,{"disambiguationData":[TD([[makeQuery(id+"F0.imprint","IMPRINT",EDGE,{"disambiguationData":[TD([[subQ2,-1.0]])],"derivedFrom":subQ1}),-1.0]])]});}
            var Q47;
            {var subQ7=sQuery(id+"F0.wireOp",EDGE,"E1.right");var subQ8=sQuery(id+"F0.wireOp",EDGE,"E1.bottom");var subQ9=makeQuery(id+"F0.imprint","INTERSECT",VERTEX,{"derivedFrom":[subQ8,subQ7]});Q47=makeQuery(id+"F0.imprint","IMPRINT",FACE,{"disambiguationData":[TD([[makeQuery(id+"F0.imprint","IMPRINT",EDGE,{"disambiguationData":[TD([[subQ9,1.0]])],"derivedFrom":subQ8}),-1.0]])]});}
            var Q48;
            {var subQ0=sQuery(id+"F0.wireOp",EDGE,"E101");var subQ1=sQuery(id+"F0.wireOp",EDGE,"E0.left");var subQ2=makeQuery(id+"F0.imprint","INTERSECT",VERTEX,{"derivedFrom":[subQ1,subQ0]});Q48=makeQuery(id+"F0.imprint","IMPRINT",FACE,{"disambiguationData":[TD([[makeQuery(id+"F0.imprint","IMPRINT",EDGE,{"disambiguationData":[TD([[subQ2,-1.0]])],"derivedFrom":subQ1}),1.0]])]});}
            var Q49;
            {var subQ0=sQuery(id+"F0.wireOp",EDGE,"E104");var subQ1=sQuery(id+"F0.wireOp",EDGE,"E1.top");var subQ2=makeQuery(id+"F0.imprint","INTERSECT",VERTEX,{"derivedFrom":[subQ1,subQ0]});Q49=makeQuery(id+"F0.imprint","IMPRINT",FACE,{"disambiguationData":[TD([[makeQuery(id+"F0.imprint","IMPRINT",EDGE,{"disambiguationData":[TD([[subQ2,-1.0]])],"derivedFrom":subQ1}),1.0]])]});}
            var Q50;
            {var subQ0=sQuery(id+"F0.wireOp",EDGE,"E92");var subQ1=sQuery(id+"F0.wireOp",EDGE,"E0.bottom");var subQ2=makeQuery(id+"F0.imprint","INTERSECT",VERTEX,{"derivedFrom":[subQ1,subQ0]});Q50=makeQuery(id+"F0.imprint","IMPRINT",FACE,{"disambiguationData":[TD([[makeQuery(id+"F0.imprint","IMPRINT",EDGE,{"disambiguationData":[TD([[subQ2,-1.0]])],"derivedFrom":subQ1}),-1.0]])]});}
            var Q51;
            {var subQ0=sQuery(id+"F0.wireOp",EDGE,"E126");var subQ1=sQuery(id+"F0.wireOp",EDGE,"E1.right");var subQ2=makeQuery(id+"F0.imprint","INTERSECT",VERTEX,{"derivedFrom":[subQ1,subQ0]});Q51=makeQuery(id+"F0.imprint","IMPRINT",FACE,{"disambiguationData":[TD([[makeQuery(id+"F0.imprint","IMPRINT",EDGE,{"disambiguationData":[TD([[subQ2,-1.0]])],"derivedFrom":subQ1}),-1.0]])]});}
            var Q52;
            {var subQ0=sQuery(id+"F0.wireOp",EDGE,"E95");var subQ1=sQuery(id+"F0.wireOp",EDGE,"E1.bottom");var subQ2=makeQuery(id+"F0.imprint","INTERSECT",VERTEX,{"derivedFrom":[subQ1,subQ0]});Q52=makeQuery(id+"F0.imprint","IMPRINT",FACE,{"disambiguationData":[TD([[makeQuery(id+"F0.imprint","IMPRINT",EDGE,{"disambiguationData":[TD([[subQ2,-1.0]])],"derivedFrom":subQ1}),-1.0]])]});}
            var Q53;
            {var subQ0=sQuery(id+"F0.wireOp",EDGE,"E63");var subQ1=sQuery(id+"F0.wireOp",EDGE,"E0.top");var subQ2=makeQuery(id+"F0.imprint","INTERSECT",VERTEX,{"derivedFrom":[subQ1,subQ0]});Q53=makeQuery(id+"F0.imprint","IMPRINT",FACE,{"disambiguationData":[TD([[makeQuery(id+"F0.imprint","IMPRINT",EDGE,{"disambiguationData":[TD([[subQ2,-1.0]])],"derivedFrom":subQ1}),1.0]])]});}
            var Q54;
            {var subQ0=sQuery(id+"F0.wireOp",EDGE,"E128");var subQ1=sQuery(id+"F0.wireOp",EDGE,"E0.right");var subQ2=makeQuery(id+"F0.imprint","INTERSECT",VERTEX,{"derivedFrom":[subQ1,subQ0]});Q54=makeQuery(id+"F0.imprint","IMPRINT",FACE,{"disambiguationData":[TD([[makeQuery(id+"F0.imprint","IMPRINT",EDGE,{"disambiguationData":[TD([[subQ2,-1.0]])],"derivedFrom":subQ1}),-1.0]])]});}
            var Q55;
            Q55=makeQuery(id+"F0.imprint","IMPRINT",FACE,{"disambiguationData":[TD([[makeQuery(id+"F0.imprint","IMPRINT",EDGE,{"derivedFrom":sQuery(id+"F0.wireOp",EDGE,"E48")}),1.0]])]});
            var Q56;
            {var subQ9=sQuery(id+"F0.wireOp",EDGE,"E1.right");var subQ10=sQuery(id+"F0.wireOp",EDGE,"E1.top");var subQ11=makeQuery(id+"F0.imprint","INTERSECT",VERTEX,{"derivedFrom":[subQ10,subQ9]});Q56=makeQuery(id+"F0.imprint","IMPRINT",FACE,{"disambiguationData":[TD([[makeQuery(id+"F0.imprint","IMPRINT",EDGE,{"disambiguationData":[TD([[subQ11,1.0]])],"derivedFrom":subQ10}),1.0]])]});}
            var Q57;
            {var subQ0=sQuery(id+"F0.wireOp",EDGE,"E123");var subQ1=sQuery(id+"F0.wireOp",EDGE,"E1.left");var subQ2=makeQuery(id+"F0.imprint","INTERSECT",VERTEX,{"derivedFrom":[subQ1,subQ0]});Q57=makeQuery(id+"F0.imprint","IMPRINT",FACE,{"disambiguationData":[TD([[makeQuery(id+"F0.imprint","IMPRINT",EDGE,{"disambiguationData":[TD([[subQ2,-1.0]])],"derivedFrom":subQ1}),1.0]])]});}
            var Q58;
            Q58=makeQuery(id+"F0.imprint","IMPRINT",FACE,{"disambiguationData":[TD([[makeQuery(id+"F0.imprint","IMPRINT",EDGE,{"derivedFrom":sQuery(id+"F0.wireOp",EDGE,"E54")}),1.0]])]});
            var Q59;
            Q59=makeQuery(id+"F0.imprint","IMPRINT",FACE,{"disambiguationData":[TD([[makeQuery(id+"F0.imprint","IMPRINT",EDGE,{"derivedFrom":sQuery(id+"F0.wireOp",EDGE,"E53")}),1.0]])]});
            var Q60;
            Q60=makeQuery(id+"F0.imprint","IMPRINT",FACE,{"disambiguationData":[TD([[makeQuery(id+"F0.imprint","IMPRINT",EDGE,{"derivedFrom":sQuery(id+"F0.wireOp",EDGE,"E56")}),1.0]])]});
            var Q61;
            Q61=makeQuery(id+"F0.imprint","IMPRINT",FACE,{"disambiguationData":[TD([[makeQuery(id+"F0.imprint","IMPRINT",EDGE,{"derivedFrom":sQuery(id+"F0.wireOp",EDGE,"E55")}),1.0]])]});
            var Q62;
            {var subQ0=sQuery(id+"F0.wireOp",EDGE,"E2.left");var subQ1=sQuery(id+"F0.wireOp",EDGE,"E2.bottom");var subQ2=makeQuery(id+"F0.imprint","INTERSECT",VERTEX,{"derivedFrom":[subQ1,subQ0]});Q62=makeQuery(id+"F0.imprint","IMPRINT",FACE,{"disambiguationData":[TD([[makeQuery(id+"F0.imprint","IMPRINT",EDGE,{"disambiguationData":[TD([[subQ2,-1.0]])],"derivedFrom":subQ1}),-1.0]])]});}
            var Q63;
            {var subQ0=sQuery(id+"F0.wireOp",EDGE,"E2.right");var subQ1=sQuery(id+"F0.wireOp",EDGE,"E2.bottom");var subQ2=makeQuery(id+"F0.imprint","INTERSECT",VERTEX,{"derivedFrom":[subQ1,subQ0]});Q63=makeQuery(id+"F0.imprint","IMPRINT",FACE,{"disambiguationData":[TD([[makeQuery(id+"F0.imprint","IMPRINT",EDGE,{"disambiguationData":[TD([[subQ2,1.0]])],"derivedFrom":subQ1}),1.0]])]});}
            var Q64;
            {var subQ0=sQuery(id+"F0.wireOp",EDGE,"E2.right");var subQ1=sQuery(id+"F0.wireOp",EDGE,"E2.top");var subQ2=makeQuery(id+"F0.imprint","INTERSECT",VERTEX,{"derivedFrom":[subQ1,subQ0]});Q64=makeQuery(id+"F0.imprint","IMPRINT",FACE,{"disambiguationData":[TD([[makeQuery(id+"F0.imprint","IMPRINT",EDGE,{"disambiguationData":[TD([[subQ2,1.0]])],"derivedFrom":subQ1}),1.0]])]});}
            var Q65;
            {var subQ0=sQuery(id+"F0.wireOp",EDGE,"E2.left");var subQ1=sQuery(id+"F0.wireOp",EDGE,"E2.bottom");var subQ2=makeQuery(id+"F0.imprint","INTERSECT",VERTEX,{"derivedFrom":[subQ1,subQ0]});Q65=makeQuery(id+"F0.imprint","IMPRINT",FACE,{"disambiguationData":[TD([[makeQuery(id+"F0.imprint","IMPRINT",EDGE,{"disambiguationData":[TD([[subQ2,-1.0]])],"derivedFrom":subQ1}),1.0]])]});}
            var Q66;
            {var subQ0=sQuery(id+"F0.wireOp",EDGE,"E2.right");var subQ1=sQuery(id+"F0.wireOp",EDGE,"E2.top");var subQ2=makeQuery(id+"F0.imprint","INTERSECT",VERTEX,{"derivedFrom":[subQ1,subQ0]});Q66=makeQuery(id+"F0.imprint","IMPRINT",FACE,{"disambiguationData":[TD([[makeQuery(id+"F0.imprint","IMPRINT",EDGE,{"disambiguationData":[TD([[subQ2,1.0]])],"derivedFrom":subQ1}),-1.0]])]});}
            var Q67;
            {var subQ0=sQuery(id+"F0.wireOp",EDGE,"E2.left");var subQ1=sQuery(id+"F0.wireOp",EDGE,"E2.top");var subQ2=makeQuery(id+"F0.imprint","INTERSECT",VERTEX,{"derivedFrom":[subQ1,subQ0]});Q67=makeQuery(id+"F0.imprint","IMPRINT",FACE,{"disambiguationData":[TD([[makeQuery(id+"F0.imprint","IMPRINT",EDGE,{"disambiguationData":[TD([[subQ2,-1.0]])],"derivedFrom":subQ1}),1.0]])]});}
            var Q68;
            Q68=makeQuery(id+"F0.imprint","IMPRINT",FACE,{"disambiguationData":[TD([[makeQuery(id+"F0.imprint","IMPRINT",EDGE,{"derivedFrom":sQuery(id+"F0.wireOp",EDGE,"E45")}),1.0]])]});
            var Q69;
            {var subQ0=sQuery(id+"F0.wireOp",EDGE,"E2.left");var subQ1=sQuery(id+"F0.wireOp",EDGE,"E2.top");var subQ2=makeQuery(id+"F0.imprint","INTERSECT",VERTEX,{"derivedFrom":[subQ1,subQ0]});Q69=makeQuery(id+"F0.imprint","IMPRINT",FACE,{"disambiguationData":[TD([[makeQuery(id+"F0.imprint","IMPRINT",EDGE,{"disambiguationData":[TD([[subQ2,-1.0]])],"derivedFrom":subQ1}),-1.0]])]});}
            var Q70;
            Q70=makeQuery(id+"F0.imprint","IMPRINT",FACE,{"disambiguationData":[TD([[makeQuery(id+"F0.imprint","IMPRINT",EDGE,{"derivedFrom":sQuery(id+"F0.wireOp",EDGE,"E46")}),1.0]])]});
            var Q71;
            Q71=makeQuery(id+"F0.imprint","IMPRINT",FACE,{"disambiguationData":[TD([[makeQuery(id+"F0.imprint","IMPRINT",EDGE,{"derivedFrom":sQuery(id+"F0.wireOp",EDGE,"E44")}),1.0]])]});
            var Q72;
            Q72=makeQuery(id+"F0.imprint","IMPRINT",FACE,{"disambiguationData":[TD([[makeQuery(id+"F0.imprint","IMPRINT",EDGE,{"derivedFrom":sQuery(id+"F0.wireOp",EDGE,"E47")}),1.0]])]});
            var Q73;
            {var subQ0=sQuery(id+"F0.wireOp",EDGE,"E2.right");var subQ1=sQuery(id+"F0.wireOp",EDGE,"E2.bottom");var subQ2=makeQuery(id+"F0.imprint","INTERSECT",VERTEX,{"derivedFrom":[subQ1,subQ0]});Q73=makeQuery(id+"F0.imprint","IMPRINT",FACE,{"disambiguationData":[TD([[makeQuery(id+"F0.imprint","IMPRINT",EDGE,{"disambiguationData":[TD([[subQ2,1.0]])],"derivedFrom":subQ1}),-1.0]])]});}
            extrude(context, id + "F1", {"entities" : qUnion([Q0, Q1, Q2, Q3, Q4, Q5, Q6, Q7, Q8, Q9, Q10, Q11, Q12, Q13, Q14, Q15, Q16, Q17, Q18, Q19, Q20, Q21, Q22, Q23, Q24, Q25, Q26, Q27, Q28, Q29, Q30, Q31, Q32, Q33, Q34, Q35, Q36, Q37, Q38, Q39, Q40, Q41, Q42, Q43, Q44, Q45, Q46, Q47, Q48, Q49, Q50, Q51, Q52, Q53, Q54, Q55, Q56, Q57, Q58, Q59, Q60, Q61, Q62, Q63, Q64, Q65, Q66, Q67, Q68, Q69, Q70, Q71, Q72, Q73]), "depth" : 6.25 * mm});
        }
        {
            var Q0;
            Q0=makeQuery(id+"F0.imprint","IMPRINT",FACE,{"disambiguationData":[TD([[makeQuery(id+"F0.imprint","IMPRINT",EDGE,{"derivedFrom":sQuery(id+"F0.wireOp",EDGE,"E41")}),1.0]])]});
            var Q1;
            Q1=makeQuery(id+"F0.imprint","IMPRINT",FACE,{"disambiguationData":[TD([[makeQuery(id+"F0.imprint","IMPRINT",EDGE,{"derivedFrom":sQuery(id+"F0.wireOp",EDGE,"E40")}),1.0]])]});
            var Q2;
            Q2=makeQuery(id+"F0.imprint","IMPRINT",FACE,{"disambiguationData":[TD([[makeQuery(id+"F0.imprint","IMPRINT",EDGE,{"derivedFrom":sQuery(id+"F0.wireOp",EDGE,"E48")}),1.0]])]});
            var Q3;
            Q3=makeQuery(id+"F0.imprint","IMPRINT",FACE,{"disambiguationData":[TD([[makeQuery(id+"F0.imprint","IMPRINT",EDGE,{"derivedFrom":sQuery(id+"F0.wireOp",EDGE,"E43")}),1.0]])]});
            var Q4;
            Q4=makeQuery(id+"F0.imprint","IMPRINT",FACE,{"disambiguationData":[TD([[makeQuery(id+"F0.imprint","IMPRINT",EDGE,{"derivedFrom":sQuery(id+"F0.wireOp",EDGE,"E42")}),1.0]])]});
            extrude(context, id + "F2", {"entities" : qUnion([Q0, Q1, Q2, Q3, Q4]), "operationType" : NewBodyOperationType.ADD, "depth" : 11.25 * mm});
        }
        {
            var Q0;
            {var subQ7=sQuery(id+"F0.wireOp",EDGE,"E0.left");var subQ8=sQuery(id+"F0.wireOp",EDGE,"E0.bottom");var subQ9=makeQuery(id+"F0.imprint","INTERSECT",VERTEX,{"derivedFrom":[subQ8,subQ7]});Q0=makeQuery(id+"F0.imprint","IMPRINT",FACE,{"disambiguationData":[TD([[makeQuery(id+"F0.imprint","IMPRINT",EDGE,{"disambiguationData":[TD([[subQ9,-1.0]])],"derivedFrom":subQ8}),-1.0]])]});}
            var Q1;
            {var subQ8=sQuery(id+"F0.wireOp",EDGE,"E1.left");var subQ9=sQuery(id+"F0.wireOp",EDGE,"E1.bottom");var subQ10=makeQuery(id+"F0.imprint","INTERSECT",VERTEX,{"derivedFrom":[subQ9,subQ8]});Q1=makeQuery(id+"F0.imprint","IMPRINT",FACE,{"disambiguationData":[TD([[makeQuery(id+"F0.imprint","IMPRINT",EDGE,{"disambiguationData":[TD([[subQ10,-1.0]])],"derivedFrom":subQ9}),-1.0]])]});}
            var Q2;
            {var subQ0=sQuery(id+"F0.wireOp",EDGE,"E100");var subQ1=sQuery(id+"F0.wireOp",EDGE,"E0.left");var subQ2=makeQuery(id+"F0.imprint","INTERSECT",VERTEX,{"derivedFrom":[subQ1,subQ0]});Q2=makeQuery(id+"F0.imprint","IMPRINT",FACE,{"disambiguationData":[TD([[makeQuery(id+"F0.imprint","IMPRINT",EDGE,{"disambiguationData":[TD([[subQ2,1.0]])],"derivedFrom":subQ1}),1.0]])]});}
            var Q3;
            {var subQ0=sQuery(id+"F0.wireOp",EDGE,"E123");var subQ1=sQuery(id+"F0.wireOp",EDGE,"E1.left");var subQ2=makeQuery(id+"F0.imprint","INTERSECT",VERTEX,{"derivedFrom":[subQ1,subQ0]});Q3=makeQuery(id+"F0.imprint","IMPRINT",FACE,{"disambiguationData":[TD([[makeQuery(id+"F0.imprint","IMPRINT",EDGE,{"disambiguationData":[TD([[subQ2,-1.0]])],"derivedFrom":subQ1}),1.0]])]});}
            var Q4;
            {var subQ0=sQuery(id+"F0.wireOp",EDGE,"E101");var subQ1=sQuery(id+"F0.wireOp",EDGE,"E0.left");var subQ2=makeQuery(id+"F0.imprint","INTERSECT",VERTEX,{"derivedFrom":[subQ1,subQ0]});Q4=makeQuery(id+"F0.imprint","IMPRINT",FACE,{"disambiguationData":[TD([[makeQuery(id+"F0.imprint","IMPRINT",EDGE,{"disambiguationData":[TD([[subQ2,-1.0]])],"derivedFrom":subQ1}),1.0]])]});}
            var Q5;
            {var subQ0=sQuery(id+"F0.wireOp",EDGE,"E101");var subQ1=sQuery(id+"F0.wireOp",EDGE,"E1.left");var subQ2=makeQuery(id+"F0.imprint","INTERSECT",VERTEX,{"derivedFrom":[subQ1,subQ0]});Q5=makeQuery(id+"F0.imprint","IMPRINT",FACE,{"disambiguationData":[TD([[makeQuery(id+"F0.imprint","IMPRINT",EDGE,{"disambiguationData":[TD([[subQ2,-1.0]])],"derivedFrom":subQ1}),1.0]])]});}
            var Q6;
            {var subQ7=sQuery(id+"F0.wireOp",EDGE,"E0.left");var subQ8=sQuery(id+"F0.wireOp",EDGE,"E0.top");var subQ9=makeQuery(id+"F0.imprint","INTERSECT",VERTEX,{"derivedFrom":[subQ8,subQ7]});Q6=makeQuery(id+"F0.imprint","IMPRINT",FACE,{"disambiguationData":[TD([[makeQuery(id+"F0.imprint","IMPRINT",EDGE,{"disambiguationData":[TD([[subQ9,-1.0]])],"derivedFrom":subQ8}),1.0]])]});}
            var Q7;
            {var subQ7=sQuery(id+"F0.wireOp",EDGE,"E1.left");var subQ8=sQuery(id+"F0.wireOp",EDGE,"E1.top");var subQ9=makeQuery(id+"F0.imprint","INTERSECT",VERTEX,{"derivedFrom":[subQ8,subQ7]});Q7=makeQuery(id+"F0.imprint","IMPRINT",FACE,{"disambiguationData":[TD([[makeQuery(id+"F0.imprint","IMPRINT",EDGE,{"disambiguationData":[TD([[subQ9,-1.0]])],"derivedFrom":subQ8}),1.0]])]});}
            var Q8;
            {var subQ5=sQuery(id+"F0.wireOp",EDGE,"E16");Q8=makeQuery(id+"F0.imprint","IMPRINT",FACE,{"disambiguationData":[TD([[makeQuery(id+"F0.imprint","IMPRINT",EDGE,{"derivedFrom":subQ5}),-1.0]])]});}
            var Q9;
            {var subQ0=sQuery(id+"F0.wireOp",EDGE,"E103");var subQ1=sQuery(id+"F0.wireOp",EDGE,"E1.top");var subQ2=makeQuery(id+"F0.imprint","INTERSECT",VERTEX,{"derivedFrom":[subQ1,subQ0]});Q9=makeQuery(id+"F0.imprint","IMPRINT",FACE,{"disambiguationData":[TD([[makeQuery(id+"F0.imprint","IMPRINT",EDGE,{"disambiguationData":[TD([[subQ2,-1.0]])],"derivedFrom":subQ1}),1.0]])]});}
            var Q10;
            {var subQ0=sQuery(id+"F0.wireOp",EDGE,"E62");var subQ1=sQuery(id+"F0.wireOp",EDGE,"E0.top");var subQ2=makeQuery(id+"F0.imprint","INTERSECT",VERTEX,{"derivedFrom":[subQ1,subQ0]});Q10=makeQuery(id+"F0.imprint","IMPRINT",FACE,{"disambiguationData":[TD([[makeQuery(id+"F0.imprint","IMPRINT",EDGE,{"disambiguationData":[TD([[subQ2,1.0]])],"derivedFrom":subQ1}),1.0]])]});}
            var Q11;
            {var subQ0=sQuery(id+"F0.wireOp",EDGE,"E63");var subQ1=sQuery(id+"F0.wireOp",EDGE,"E0.top");var subQ2=makeQuery(id+"F0.imprint","INTERSECT",VERTEX,{"derivedFrom":[subQ1,subQ0]});Q11=makeQuery(id+"F0.imprint","IMPRINT",FACE,{"disambiguationData":[TD([[makeQuery(id+"F0.imprint","IMPRINT",EDGE,{"disambiguationData":[TD([[subQ2,-1.0]])],"derivedFrom":subQ1}),1.0]])]});}
            var Q12;
            {var subQ0=sQuery(id+"F0.wireOp",EDGE,"E63");var subQ1=sQuery(id+"F0.wireOp",EDGE,"E1.top");var subQ2=makeQuery(id+"F0.imprint","INTERSECT",VERTEX,{"derivedFrom":[subQ1,subQ0]});Q12=makeQuery(id+"F0.imprint","IMPRINT",FACE,{"disambiguationData":[TD([[makeQuery(id+"F0.imprint","IMPRINT",EDGE,{"disambiguationData":[TD([[subQ2,-1.0]])],"derivedFrom":subQ1}),1.0]])]});}
            var Q13;
            {var subQ9=sQuery(id+"F0.wireOp",EDGE,"E1.right");var subQ10=sQuery(id+"F0.wireOp",EDGE,"E1.top");var subQ11=makeQuery(id+"F0.imprint","INTERSECT",VERTEX,{"derivedFrom":[subQ10,subQ9]});Q13=makeQuery(id+"F0.imprint","IMPRINT",FACE,{"disambiguationData":[TD([[makeQuery(id+"F0.imprint","IMPRINT",EDGE,{"disambiguationData":[TD([[subQ11,1.0]])],"derivedFrom":subQ10}),1.0]])]});}
            var Q14;
            {var subQ7=sQuery(id+"F0.wireOp",EDGE,"E0.right");var subQ8=sQuery(id+"F0.wireOp",EDGE,"E0.top");var subQ9=makeQuery(id+"F0.imprint","INTERSECT",VERTEX,{"derivedFrom":[subQ8,subQ7]});Q14=makeQuery(id+"F0.imprint","IMPRINT",FACE,{"disambiguationData":[TD([[makeQuery(id+"F0.imprint","IMPRINT",EDGE,{"disambiguationData":[TD([[subQ9,1.0]])],"derivedFrom":subQ8}),1.0]])]});}
            var Q15;
            {var subQ5=sQuery(id+"F0.wireOp",EDGE,"E17");Q15=makeQuery(id+"F0.imprint","IMPRINT",FACE,{"disambiguationData":[TD([[makeQuery(id+"F0.imprint","IMPRINT",EDGE,{"derivedFrom":subQ5}),-1.0]])]});}
            var Q16;
            {var subQ0=sQuery(id+"F0.wireOp",EDGE,"E99");var subQ1=sQuery(id+"F0.wireOp",EDGE,"E0.right");var subQ2=makeQuery(id+"F0.imprint","INTERSECT",VERTEX,{"derivedFrom":[subQ1,subQ0]});Q16=makeQuery(id+"F0.imprint","IMPRINT",FACE,{"disambiguationData":[TD([[makeQuery(id+"F0.imprint","IMPRINT",EDGE,{"disambiguationData":[TD([[subQ2,-1.0]])],"derivedFrom":subQ1}),-1.0]])]});}
            var Q17;
            {var subQ0=sQuery(id+"F0.wireOp",EDGE,"E99");var subQ1=sQuery(id+"F0.wireOp",EDGE,"E1.right");var subQ2=makeQuery(id+"F0.imprint","INTERSECT",VERTEX,{"derivedFrom":[subQ1,subQ0]});Q17=makeQuery(id+"F0.imprint","IMPRINT",FACE,{"disambiguationData":[TD([[makeQuery(id+"F0.imprint","IMPRINT",EDGE,{"disambiguationData":[TD([[subQ2,-1.0]])],"derivedFrom":subQ1}),-1.0]])]});}
            var Q18;
            {var subQ0=sQuery(id+"F0.wireOp",EDGE,"E153");var subQ1=sQuery(id+"F0.wireOp",EDGE,"E1.right");var subQ2=makeQuery(id+"F0.imprint","INTERSECT",VERTEX,{"derivedFrom":[subQ1,subQ0]});Q18=makeQuery(id+"F0.imprint","IMPRINT",FACE,{"disambiguationData":[TD([[makeQuery(id+"F0.imprint","IMPRINT",EDGE,{"disambiguationData":[TD([[subQ2,-1.0]])],"derivedFrom":subQ1}),-1.0]])]});}
            var Q19;
            {var subQ0=sQuery(id+"F0.wireOp",EDGE,"E98");var subQ1=sQuery(id+"F0.wireOp",EDGE,"E0.right");var subQ2=makeQuery(id+"F0.imprint","INTERSECT",VERTEX,{"derivedFrom":[subQ1,subQ0]});Q19=makeQuery(id+"F0.imprint","IMPRINT",FACE,{"disambiguationData":[TD([[makeQuery(id+"F0.imprint","IMPRINT",EDGE,{"disambiguationData":[TD([[subQ2,1.0]])],"derivedFrom":subQ1}),-1.0]])]});}
            var Q20;
            {var subQ7=sQuery(id+"F0.wireOp",EDGE,"E1.right");var subQ8=sQuery(id+"F0.wireOp",EDGE,"E1.bottom");var subQ9=makeQuery(id+"F0.imprint","INTERSECT",VERTEX,{"derivedFrom":[subQ8,subQ7]});Q20=makeQuery(id+"F0.imprint","IMPRINT",FACE,{"disambiguationData":[TD([[makeQuery(id+"F0.imprint","IMPRINT",EDGE,{"disambiguationData":[TD([[subQ9,1.0]])],"derivedFrom":subQ8}),-1.0]])]});}
            var Q21;
            {var subQ5=sQuery(id+"F0.wireOp",EDGE,"E0.right");var subQ9=sQuery(id+"F0.wireOp",EDGE,"E0.bottom");var subQ10=makeQuery(id+"F0.imprint","INTERSECT",VERTEX,{"derivedFrom":[subQ9,subQ5]});Q21=makeQuery(id+"F0.imprint","IMPRINT",FACE,{"disambiguationData":[TD([[makeQuery(id+"F0.imprint","IMPRINT",EDGE,{"disambiguationData":[TD([[subQ10,1.0]])],"derivedFrom":subQ9}),-1.0]])]});}
            var Q22;
            {var subQ0=sQuery(id+"F0.wireOp",EDGE,"E18");Q22=makeQuery(id+"F0.imprint","IMPRINT",FACE,{"disambiguationData":[TD([[makeQuery(id+"F0.imprint","IMPRINT",EDGE,{"derivedFrom":subQ0}),-1.0]])]});}
            var Q23;
            {var subQ0=sQuery(id+"F0.wireOp",EDGE,"E95");var subQ1=sQuery(id+"F0.wireOp",EDGE,"E1.bottom");var subQ2=makeQuery(id+"F0.imprint","INTERSECT",VERTEX,{"derivedFrom":[subQ1,subQ0]});Q23=makeQuery(id+"F0.imprint","IMPRINT",FACE,{"disambiguationData":[TD([[makeQuery(id+"F0.imprint","IMPRINT",EDGE,{"disambiguationData":[TD([[subQ2,-1.0]])],"derivedFrom":subQ1}),-1.0]])]});}
            var Q24;
            {var subQ0=sQuery(id+"F0.wireOp",EDGE,"E95");var subQ1=sQuery(id+"F0.wireOp",EDGE,"E0.bottom");var subQ2=makeQuery(id+"F0.imprint","INTERSECT",VERTEX,{"derivedFrom":[subQ1,subQ0]});Q24=makeQuery(id+"F0.imprint","IMPRINT",FACE,{"disambiguationData":[TD([[makeQuery(id+"F0.imprint","IMPRINT",EDGE,{"disambiguationData":[TD([[subQ2,-1.0]])],"derivedFrom":subQ1}),-1.0]])]});}
            var Q25;
            {var subQ0=sQuery(id+"F0.wireOp",EDGE,"E93");var subQ1=sQuery(id+"F0.wireOp",EDGE,"E0.bottom");var subQ2=makeQuery(id+"F0.imprint","INTERSECT",VERTEX,{"derivedFrom":[subQ1,subQ0]});Q25=makeQuery(id+"F0.imprint","IMPRINT",FACE,{"disambiguationData":[TD([[makeQuery(id+"F0.imprint","IMPRINT",EDGE,{"disambiguationData":[TD([[subQ2,-1.0]])],"derivedFrom":subQ1}),-1.0]])]});}
            var Q26;
            {var subQ0=sQuery(id+"F0.wireOp",EDGE,"E93");var subQ1=sQuery(id+"F0.wireOp",EDGE,"E1.bottom");var subQ2=makeQuery(id+"F0.imprint","INTERSECT",VERTEX,{"derivedFrom":[subQ1,subQ0]});Q26=makeQuery(id+"F0.imprint","IMPRINT",FACE,{"disambiguationData":[TD([[makeQuery(id+"F0.imprint","IMPRINT",EDGE,{"disambiguationData":[TD([[subQ2,-1.0]])],"derivedFrom":subQ1}),-1.0]])]});}
            var Q27;
            {var subQ0=sQuery(id+"F0.wireOp",EDGE,"E19");Q27=makeQuery(id+"F0.imprint","IMPRINT",FACE,{"disambiguationData":[TD([[makeQuery(id+"F0.imprint","IMPRINT",EDGE,{"derivedFrom":subQ0}),-1.0]])]});}
            extrude(context, id + "F3", {"entities" : qUnion([Q0, Q1, Q2, Q3, Q4, Q5, Q6, Q7, Q8, Q9, Q10, Q11, Q12, Q13, Q14, Q15, Q16, Q17, Q18, Q19, Q20, Q21, Q22, Q23, Q24, Q25, Q26, Q27]), "operationType" : NewBodyOperationType.ADD, "depth" : 31.25 * mm});
        }
        {
            var Q0;
            {var subQ0=sQuery(id+"F0.wireOp",EDGE,"E94");var subQ1=sQuery(id+"F0.wireOp",EDGE,"E0.bottom");var subQ2=makeQuery(id+"F0.imprint","INTERSECT",VERTEX,{"derivedFrom":[subQ1,subQ0]});Q0=makeQuery(id+"F0.imprint","IMPRINT",FACE,{"disambiguationData":[TD([[makeQuery(id+"F0.imprint","IMPRINT",EDGE,{"disambiguationData":[TD([[subQ2,-1.0]])],"derivedFrom":subQ1}),-1.0]])]});}
            var Q1;
            {var subQ0=sQuery(id+"F0.wireOp",EDGE,"E94");var subQ1=sQuery(id+"F0.wireOp",EDGE,"E1.bottom");var subQ2=makeQuery(id+"F0.imprint","INTERSECT",VERTEX,{"derivedFrom":[subQ1,subQ0]});Q1=makeQuery(id+"F0.imprint","IMPRINT",FACE,{"disambiguationData":[TD([[makeQuery(id+"F0.imprint","IMPRINT",EDGE,{"disambiguationData":[TD([[subQ2,-1.0]])],"derivedFrom":subQ1}),-1.0]])]});}
            var Q2;
            {var subQ0=sQuery(id+"F0.wireOp",EDGE,"E98");var subQ1=sQuery(id+"F0.wireOp",EDGE,"E0.right");var subQ2=makeQuery(id+"F0.imprint","INTERSECT",VERTEX,{"derivedFrom":[subQ1,subQ0]});Q2=makeQuery(id+"F0.imprint","IMPRINT",FACE,{"disambiguationData":[TD([[makeQuery(id+"F0.imprint","IMPRINT",EDGE,{"disambiguationData":[TD([[subQ2,-1.0]])],"derivedFrom":subQ1}),-1.0]])]});}
            var Q3;
            {var subQ0=sQuery(id+"F0.wireOp",EDGE,"E98");var subQ1=sQuery(id+"F0.wireOp",EDGE,"E1.right");var subQ2=makeQuery(id+"F0.imprint","INTERSECT",VERTEX,{"derivedFrom":[subQ1,subQ0]});Q3=makeQuery(id+"F0.imprint","IMPRINT",FACE,{"disambiguationData":[TD([[makeQuery(id+"F0.imprint","IMPRINT",EDGE,{"disambiguationData":[TD([[subQ2,-1.0]])],"derivedFrom":subQ1}),-1.0]])]});}
            var Q4;
            {var subQ0=sQuery(id+"F0.wireOp",EDGE,"E100");var subQ1=sQuery(id+"F0.wireOp",EDGE,"E1.left");var subQ2=makeQuery(id+"F0.imprint","INTERSECT",VERTEX,{"derivedFrom":[subQ1,subQ0]});Q4=makeQuery(id+"F0.imprint","IMPRINT",FACE,{"disambiguationData":[TD([[makeQuery(id+"F0.imprint","IMPRINT",EDGE,{"disambiguationData":[TD([[subQ2,-1.0]])],"derivedFrom":subQ1}),1.0]])]});}
            var Q5;
            {var subQ0=sQuery(id+"F0.wireOp",EDGE,"E100");var subQ1=sQuery(id+"F0.wireOp",EDGE,"E0.left");var subQ2=makeQuery(id+"F0.imprint","INTERSECT",VERTEX,{"derivedFrom":[subQ1,subQ0]});Q5=makeQuery(id+"F0.imprint","IMPRINT",FACE,{"disambiguationData":[TD([[makeQuery(id+"F0.imprint","IMPRINT",EDGE,{"disambiguationData":[TD([[subQ2,-1.0]])],"derivedFrom":subQ1}),1.0]])]});}
            var Q6;
            {var subQ0=sQuery(id+"F0.wireOp",EDGE,"E62");var subQ1=sQuery(id+"F0.wireOp",EDGE,"E1.top");var subQ2=makeQuery(id+"F0.imprint","INTERSECT",VERTEX,{"derivedFrom":[subQ1,subQ0]});Q6=makeQuery(id+"F0.imprint","IMPRINT",FACE,{"disambiguationData":[TD([[makeQuery(id+"F0.imprint","IMPRINT",EDGE,{"disambiguationData":[TD([[subQ2,-1.0]])],"derivedFrom":subQ1}),1.0]])]});}
            var Q7;
            {var subQ0=sQuery(id+"F0.wireOp",EDGE,"E62");var subQ1=sQuery(id+"F0.wireOp",EDGE,"E0.top");var subQ2=makeQuery(id+"F0.imprint","INTERSECT",VERTEX,{"derivedFrom":[subQ1,subQ0]});Q7=makeQuery(id+"F0.imprint","IMPRINT",FACE,{"disambiguationData":[TD([[makeQuery(id+"F0.imprint","IMPRINT",EDGE,{"disambiguationData":[TD([[subQ2,-1.0]])],"derivedFrom":subQ1}),1.0]])]});}
            extrude(context, id + "F4", {"entities" : qUnion([Q0, Q1, Q2, Q3, Q4, Q5, Q6, Q7]), "operationType" : NewBodyOperationType.ADD, "depth" : 25.25 * mm});
        }
    });
